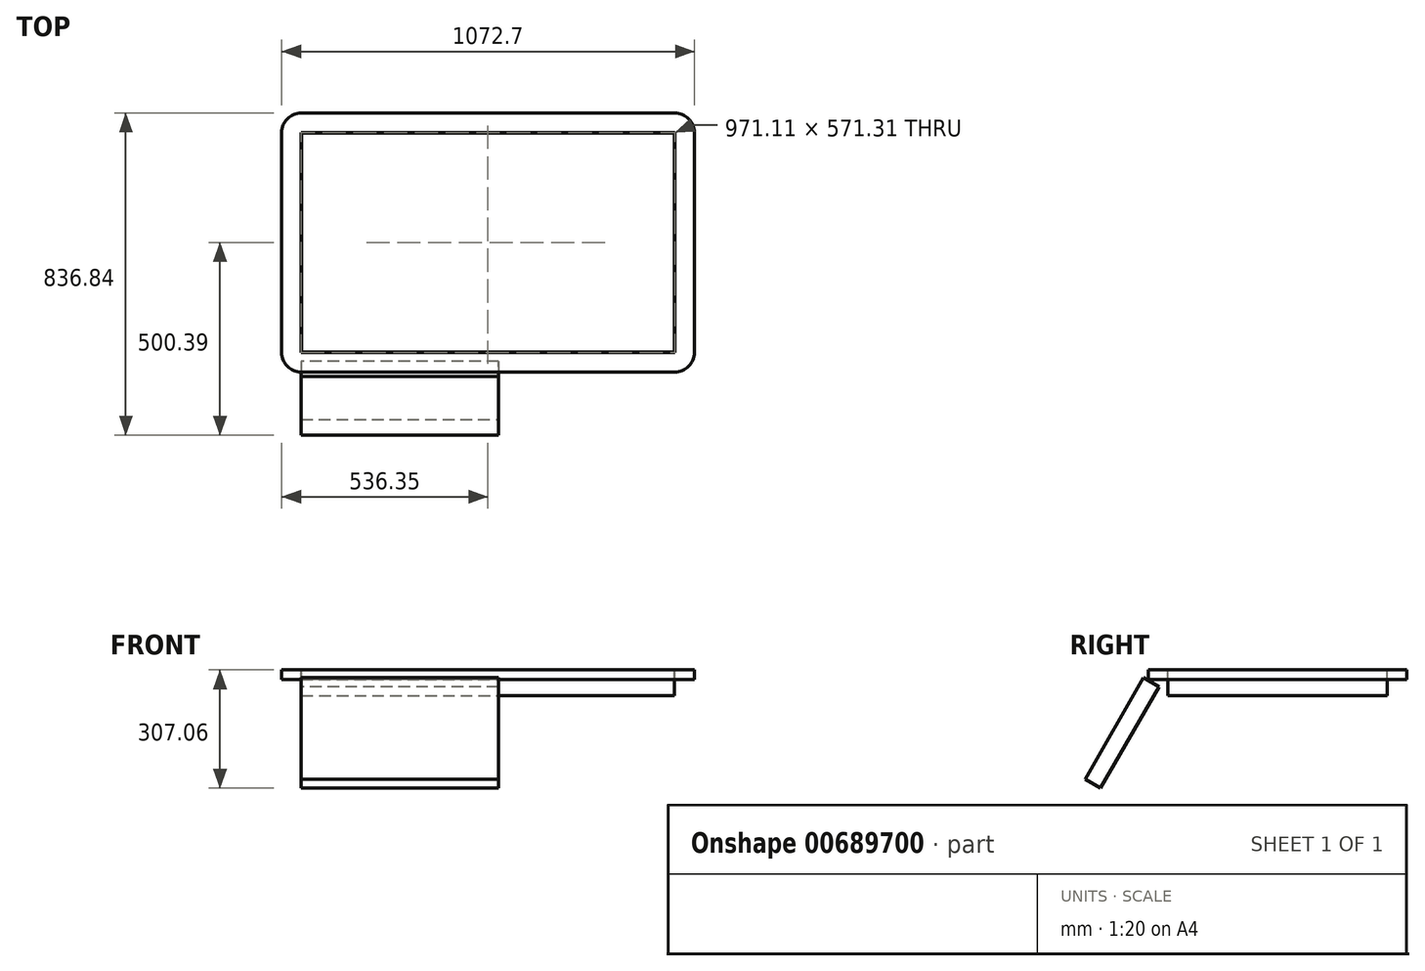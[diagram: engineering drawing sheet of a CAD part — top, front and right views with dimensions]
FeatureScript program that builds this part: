
annotation { "Feature Type Name" : "Feature", "Feature Type Description" : "" }
export const myFeature = defineFeature(function(context is Context, id is Id, definition is map)
    precondition{}
    {
        {
            var Q0;
            Q0=qCreatedBy(makeId("Top.planeOp"),FACE);
            var sketch = newSketch(context, id + "F0", { "sketchPlane" : qUnion([Q0])});
            skLineSegment(sketch, "E0.bottom", {"start": v(-484.76, 284.86) * mm, "end": v(484.76, 284.86) * mm});
            skLineSegment(sketch, "E0.top", {"start": v(-484.76, -284.86) * mm, "end": v(484.76, -284.86) * mm});
            skLineSegment(sketch, "E0.left", {"start": v(-484.76, 284.86) * mm, "end": v(-484.76, -284.86) * mm});
            skLineSegment(sketch, "E0.right", {"start": v(484.76, 284.86) * mm, "end": v(484.76, -284.86) * mm});
            skLineSegment(sketch, "E1", {"start": v(-484.76, 0) * mm, "end": v(0, 0) * mm, "construction": true});
            skLineSegment(sketch, "E2", {"start": v(0, 0) * mm, "end": v(0, 284.86) * mm, "construction": true});
            skSolve(sketch);
        }
        {
            var Q0;
            Q0 = qSketchRegion(id + "F0", true);
            extrude(context, id + "F1", {"entities" : qUnion([Q0]), "oppositeDirection" : true, "depth" : 67.06 * mm, "offsetDistance" : 25.4 * mm});
        }
        {
            var Q0;
            Q0=qCreatedBy(makeId("Top.planeOp"),FACE);
            var sketch = newSketch(context, id + "F2", { "sketchPlane" : qUnion([Q0])});
            skLineSegment(sketch, "E3.0", {"start": v(-485.55, 285.65) * mm, "end": v(-485.55, -285.65) * mm});
            skLineSegment(sketch, "E3.1", {"start": v(485.55, 285.65) * mm, "end": v(-485.55, 285.65) * mm});
            skLineSegment(sketch, "E3.2", {"start": v(485.55, -285.65) * mm, "end": v(485.55, 285.65) * mm});
            skLineSegment(sketch, "E3.3", {"start": v(-485.55, -285.65) * mm, "end": v(485.55, -285.65) * mm});
            skLineSegment(sketch, "E4.0", {"start": v(485.55, 336.45) * mm, "end": v(-485.55, 336.45) * mm});
            skLineSegment(sketch, "E4.1", {"start": v(536.35, -285.65) * mm, "end": v(536.35, 285.65) * mm});
            skLineSegment(sketch, "E4.2", {"start": v(-485.55, -336.45) * mm, "end": v(485.55, -336.45) * mm});
            skLineSegment(sketch, "E4.3", {"start": v(-536.35, 285.65) * mm, "end": v(-536.35, -285.65) * mm});
            skPoint(sketch, "E5.visualSharp", {"position": v(-536.35, 336.45) * mm});
            skArc(sketch, "E5.filletArc", {"start": v(-485.55, 336.45) * mm, "mid": v(-521.47, 321.58) * mm, "end": v(-536.35, 285.65) * mm});
            skPoint(sketch, "E6.visualSharp", {"position": v(-536.35, -336.45) * mm});
            skArc(sketch, "E6.filletArc", {"start": v(-536.35, -285.65) * mm, "mid": v(-521.47, -321.58) * mm, "end": v(-485.55, -336.45) * mm});
            skPoint(sketch, "E7.visualSharp", {"position": v(536.35, -336.45) * mm});
            skArc(sketch, "E7.filletArc", {"start": v(485.55, -336.45) * mm, "mid": v(521.47, -321.58) * mm, "end": v(536.35, -285.65) * mm});
            skPoint(sketch, "E8.visualSharp", {"position": v(536.35, 336.45) * mm});
            skArc(sketch, "E8.filletArc", {"start": v(536.35, 285.65) * mm, "mid": v(521.47, 321.58) * mm, "end": v(485.55, 336.45) * mm});
            skSolve(sketch);
        }
        {
            var Q0;
            Q0 = qSketchRegion(id + "F2", true);
            extrude(context, id + "F3", {"entities" : qUnion([Q0]), "oppositeDirection" : true, "depth" : 25.4 * mm, "offsetDistance" : 25.4 * mm});
        }
        {
            var Q0;
            Q0=makeQuery(id+"F3.opExtrude","SWEPT_FACE",FACE,{"disambiguationData":[OSD([sQuery(id+"F2.wireOp",EDGE,"E4.2")])]});
            var Q1;
            Q1=makeQuery(id+"F3.opExtrude","CAP_EDGE",EDGE,{"disambiguationData":[OSD([sQuery(id+"F2.wireOp",EDGE,"E4.2")])],"isStart":true});
            cPlane(context, id + "F4", {"entities" : qUnion([Q0, Q1]), "cplaneType" : CPlaneType.LINE_ANGLE, "offset" : 25.4 * mm, "angle" : 30 * degree, "oppositeDirection" : true, "width" : 152.4 * mm, "height" : 152.4 * mm});
        }
        {
            var Q0;
            Q0=qCreatedBy(id+"F4.planeOp",FACE);
            var sketch = newSketch(context, id + "F5", { "sketchPlane" : qUnion([Q0])});
            skLineSegment(sketch, "E9", {"start": v(485.55, -191.81) * mm, "end": v(485.55, -496.1) * mm});
            skLineSegment(sketch, "E10", {"start": v(485.55, -496.1) * mm, "end": v(-27.27, -496.1) * mm});
            skLineSegment(sketch, "E11", {"start": v(-27.27, -496.1) * mm, "end": v(-27.27, -191.81) * mm});
            skLineSegment(sketch, "E12", {"start": v(-27.27, -191.81) * mm, "end": v(485.55, -191.81) * mm});
            skSolve(sketch);
        }
        {
            var Q0;
            Q0 = qSketchRegion(id + "F5", true);
            extrude(context, id + "F6", {"entities" : qUnion([Q0]), "depth" : 46.23 * mm, "offsetDistance" : 25.4 * mm});
        }
        {
            var Q0;
            Q0=qCreatedBy(makeId("Top.planeOp"),FACE);
            var Q1;
            Q1=makeQuery(id+"F6.opExtrude","CAP_EDGE",EDGE,{"disambiguationData":[OSD([sQuery(id+"F5.wireOp",EDGE,"E10")])],"isStart":true});
            cPlane(context, id + "F7", {"entities" : qUnion([Q0, Q1]), "cplaneType" : CPlaneType.LINE_ANGLE, "offset" : 25.4 * mm, "angle" : 0 * degree, "width" : 152.4 * mm, "height" : 152.4 * mm});
        }
    });
